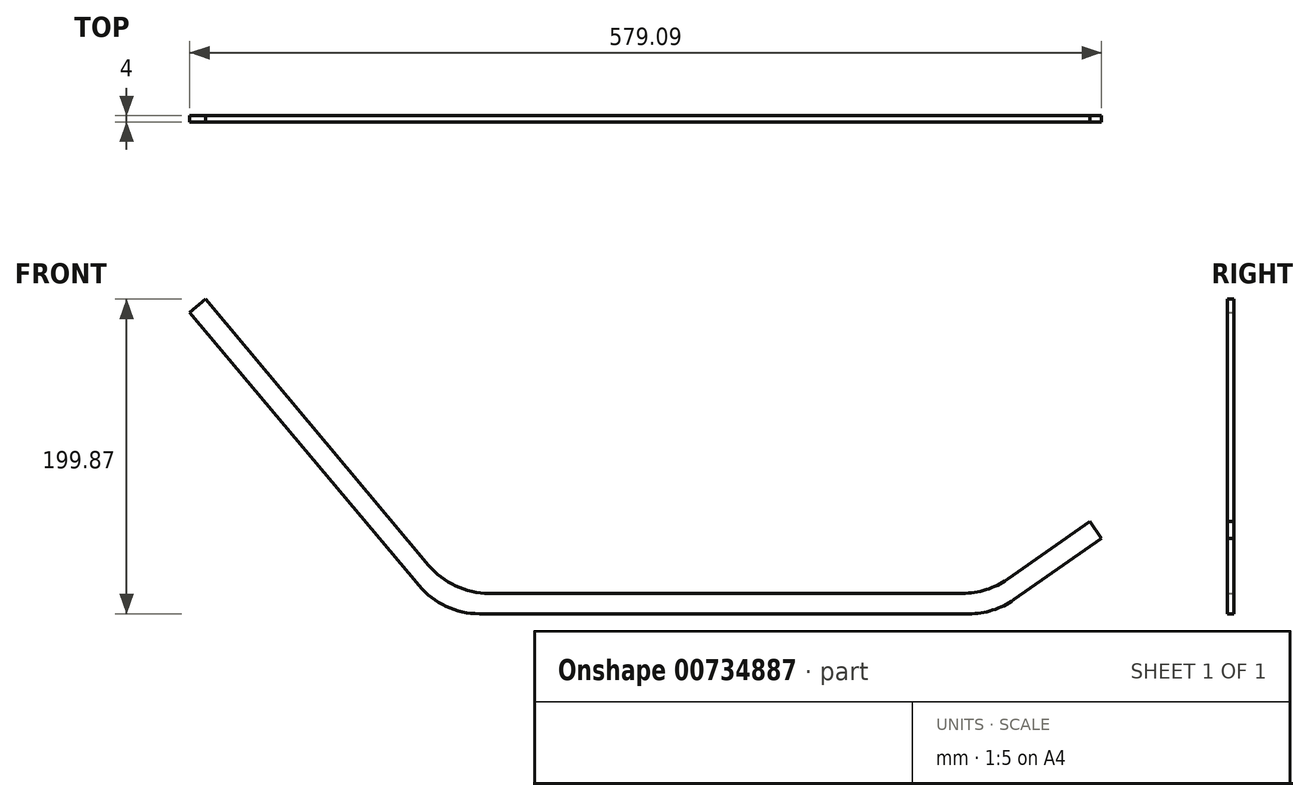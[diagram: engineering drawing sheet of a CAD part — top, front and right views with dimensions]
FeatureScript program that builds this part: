
annotation { "Feature Type Name" : "Feature", "Feature Type Description" : "" }
export const myFeature = defineFeature(function(context is Context, id is Id, definition is map)
    precondition{}
    {
        {
            var Q0;
            Q0=qCreatedBy(makeId("Front.planeOp"),FACE);
            var sketch = newSketch(context, id + "F0", { "sketchPlane" : qUnion([Q0])});
            skLineSegment(sketch, "E0.bottom", {"start": v(12.15, -12.98) * mm, "end": v(323.07, -12.98) * mm});
            skLineSegment(sketch, "E0.top", {"start": v(18.2, 0.02) * mm, "end": v(318.97, 0.02) * mm});
            skLineSegment(sketch, "E1", {"start": v(-26.16, 4.88) * mm, "end": v(-171.87, 178.53) * mm});
            skLineSegment(sketch, "E2", {"start": v(-11.17, -12.98) * mm, "end": v(-477.52, -12.98) * mm, "construction": true});
            skLineSegment(sketch, "E3", {"start": v(351.74, -3.93) * mm, "end": v(407.22, 34.91) * mm});
            skLineSegment(sketch, "E4", {"start": v(299.31, -12.98) * mm, "end": v(338.83, -12.98) * mm, "construction": true});
            skLineSegment(sketch, "E5.0", {"start": v(-20.1, 17.88) * mm, "end": v(-161.9, 186.9) * mm});
            skLineSegment(sketch, "E6.0", {"start": v(347.64, 9.07) * mm, "end": v(399.76, 45.56) * mm});
            skLineSegment(sketch, "E7", {"start": v(-171.87, 178.53) * mm, "end": v(-161.9, 186.9) * mm});
            skLineSegment(sketch, "E8", {"start": v(399.76, 45.56) * mm, "end": v(407.22, 34.91) * mm});
            skPoint(sketch, "E9.visualSharp", {"position": v(-11.17, -12.98) * mm});
            skArc(sketch, "E9.filletArc", {"start": v(-26.16, 4.88) * mm, "mid": v(-8.99, -8.3) * mm, "end": v(12.15, -12.98) * mm});
            skPoint(sketch, "E10.visualSharp", {"position": v(-5.1, 0.02) * mm});
            skArc(sketch, "E10.filletArc", {"start": v(-20.1, 17.88) * mm, "mid": v(-2.92, 4.7) * mm, "end": v(18.2, 0.02) * mm});
            skPoint(sketch, "E11.visualSharp", {"position": v(334.73, 0.02) * mm});
            skArc(sketch, "E11.filletArc", {"start": v(318.97, 0.02) * mm, "mid": v(334, 2.34) * mm, "end": v(347.64, 9.07) * mm});
            skPoint(sketch, "E12.visualSharp", {"position": v(338.83, -12.98) * mm});
            skArc(sketch, "E12.filletArc", {"start": v(323.07, -12.98) * mm, "mid": v(338.1, -10.66) * mm, "end": v(351.74, -3.93) * mm});
            skSolve(sketch);
        }
        {
            var Q0;
            Q0 = qSketchRegion(id + "F0", true);
            extrude(context, id + "F1", {"entities" : qUnion([Q0]), "depth" : 4 * mm, "offsetDistance" : 25 * mm});
        }
    });
